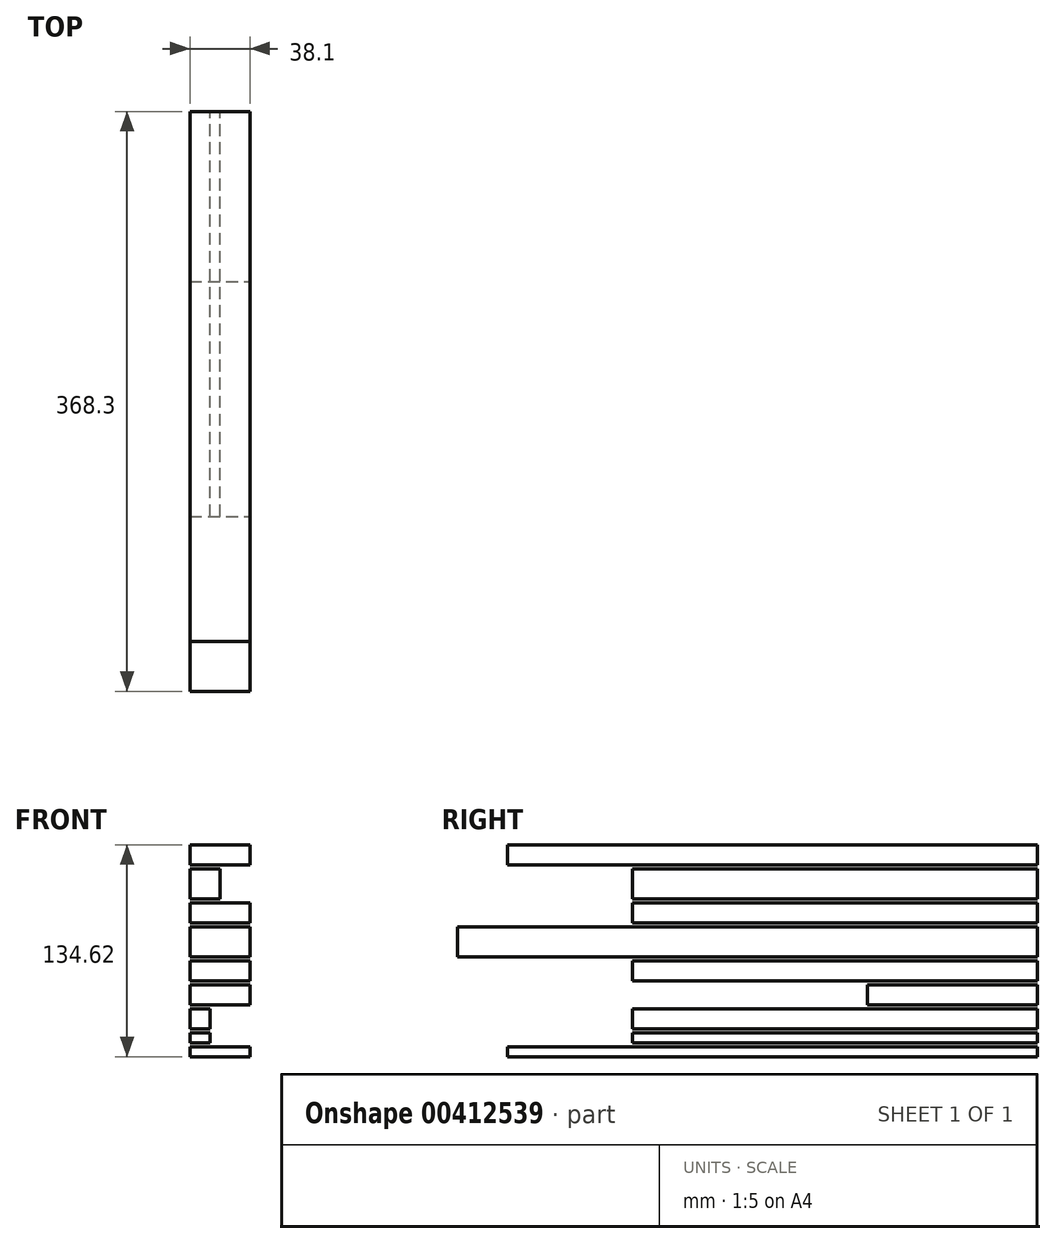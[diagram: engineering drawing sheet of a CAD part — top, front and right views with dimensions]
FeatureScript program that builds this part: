
annotation { "Feature Type Name" : "Feature", "Feature Type Description" : "" }
export const myFeature = defineFeature(function(context is Context, id is Id, definition is map)
    precondition{}
    {
        {
            var Q0;
            Q0=qCreatedBy(makeId("Front.planeOp"),FACE);
            var sketch = newSketch(context, id + "F0", { "sketchPlane" : qUnion([Q0])});
            skLineSegment(sketch, "E0.bottom", {"start": v(0, 0) * mm, "end": v(38.1, 0) * mm});
            skLineSegment(sketch, "E0.top", {"start": v(0, 19.05) * mm, "end": v(38.1, 19.05) * mm});
            skLineSegment(sketch, "E0.left", {"start": v(0, 0) * mm, "end": v(0, 19.05) * mm});
            skLineSegment(sketch, "E0.right", {"start": v(38.1, 0) * mm, "end": v(38.1, 19.05) * mm});
            skSolve(sketch);
        }
        {
            var Q0;
            Q0 = qSketchRegion(id + "F0", true);
            extrude(context, id + "F1", {"entities" : qUnion([Q0]), "depth" : 368.3 * mm});
        }
        {
            var Q0;
            Q0=qCreatedBy(makeId("Front.planeOp"),FACE);
            var sketch = newSketch(context, id + "F2", { "sketchPlane" : qUnion([Q0])});
            skLineSegment(sketch, "E1.bottom", {"start": v(0, 21.59) * mm, "end": v(38.1, 21.59) * mm});
            skLineSegment(sketch, "E1.top", {"start": v(0, 34.3) * mm, "end": v(38.1, 34.3) * mm});
            skLineSegment(sketch, "E1.left", {"start": v(0, 21.59) * mm, "end": v(0, 34.3) * mm});
            skLineSegment(sketch, "E1.right", {"start": v(38.1, 21.59) * mm, "end": v(38.1, 34.3) * mm});
            skSolve(sketch);
        }
        {
            var Q0;
            Q0 = qSketchRegion(id + "F2", true);
            extrude(context, id + "F3", {"entities" : qUnion([Q0]), "depth" : 257.18 * mm});
        }
        {
            var Q0;
            Q0=qCreatedBy(makeId("Front.planeOp"),FACE);
            var sketch = newSketch(context, id + "F4", { "sketchPlane" : qUnion([Q0])});
            skLineSegment(sketch, "E2.bottom", {"start": v(0, 36.83) * mm, "end": v(19.05, 36.83) * mm});
            skLineSegment(sketch, "E2.top", {"start": v(0, 55.88) * mm, "end": v(19.05, 55.88) * mm});
            skLineSegment(sketch, "E2.left", {"start": v(0, 36.83) * mm, "end": v(0, 55.88) * mm});
            skLineSegment(sketch, "E2.right", {"start": v(19.05, 36.83) * mm, "end": v(19.05, 55.88) * mm});
            skSolve(sketch);
        }
        {
            var Q0;
            Q0 = qSketchRegion(id + "F4", true);
            extrude(context, id + "F5", {"entities" : qUnion([Q0]), "depth" : 257.18 * mm});
        }
        {
            var Q0;
            Q0=qCreatedBy(makeId("Front.planeOp"),FACE);
            var sketch = newSketch(context, id + "F6", { "sketchPlane" : qUnion([Q0])});
            skLineSegment(sketch, "E3.bottom", {"start": v(0, 71.12) * mm, "end": v(38.1, 71.12) * mm});
            skLineSegment(sketch, "E3.top", {"start": v(0, 58.42) * mm, "end": v(38.1, 58.42) * mm});
            skLineSegment(sketch, "E3.left", {"start": v(0, 71.12) * mm, "end": v(0, 58.42) * mm});
            skLineSegment(sketch, "E3.right", {"start": v(38.1, 71.12) * mm, "end": v(38.1, 58.42) * mm});
            skSolve(sketch);
        }
        {
            var Q0;
            Q0 = qSketchRegion(id + "F6", true);
            extrude(context, id + "F7", {"entities" : qUnion([Q0]), "depth" : 336.55 * mm});
        }
        {
            var Q0;
            Q0=qCreatedBy(makeId("Front.planeOp"),FACE);
            var sketch = newSketch(context, id + "F8", { "sketchPlane" : qUnion([Q0])});
            skLineSegment(sketch, "E4.bottom", {"start": v(0, -2.54) * mm, "end": v(38.1, -2.54) * mm});
            skLineSegment(sketch, "E4.top", {"start": v(0, -15.24) * mm, "end": v(38.1, -15.24) * mm});
            skLineSegment(sketch, "E4.left", {"start": v(0, -2.54) * mm, "end": v(0, -15.24) * mm});
            skLineSegment(sketch, "E4.right", {"start": v(38.1, -2.54) * mm, "end": v(38.1, -15.24) * mm});
            skSolve(sketch);
        }
        {
            var Q0;
            Q0 = qSketchRegion(id + "F8", true);
            extrude(context, id + "F9", {"entities" : qUnion([Q0]), "depth" : 257.18 * mm});
        }
        {
            var Q0;
            Q0=qCreatedBy(makeId("Front.planeOp"),FACE);
            var sketch = newSketch(context, id + "F10", { "sketchPlane" : qUnion([Q0])});
            skLineSegment(sketch, "E5.bottom", {"start": v(0, -17.78) * mm, "end": v(38.1, -17.78) * mm});
            skLineSegment(sketch, "E5.top", {"start": v(0, -30.48) * mm, "end": v(38.1, -30.48) * mm});
            skLineSegment(sketch, "E5.left", {"start": v(0, -17.78) * mm, "end": v(0, -30.48) * mm});
            skLineSegment(sketch, "E5.right", {"start": v(38.1, -17.78) * mm, "end": v(38.1, -30.48) * mm});
            skSolve(sketch);
        }
        {
            var Q0;
            Q0 = qSketchRegion(id + "F10", true);
            extrude(context, id + "F11", {"entities" : qUnion([Q0]), "depth" : 107.95 * mm});
        }
        {
            var Q0;
            Q0=qCreatedBy(makeId("Front.planeOp"),FACE);
            var sketch = newSketch(context, id + "F12", { "sketchPlane" : qUnion([Q0])});
            skLineSegment(sketch, "E6.bottom", {"start": v(0, -33.02) * mm, "end": v(12.7, -33.02) * mm});
            skLineSegment(sketch, "E6.top", {"start": v(0, -45.72) * mm, "end": v(12.7, -45.72) * mm});
            skLineSegment(sketch, "E6.left", {"start": v(0, -33.02) * mm, "end": v(0, -45.72) * mm});
            skLineSegment(sketch, "E6.right", {"start": v(12.7, -33.02) * mm, "end": v(12.7, -45.72) * mm});
            skSolve(sketch);
        }
        {
            var Q0;
            Q0 = qSketchRegion(id + "F12", true);
            extrude(context, id + "F13", {"entities" : qUnion([Q0]), "depth" : 257.18 * mm});
        }
        {
            var Q0;
            Q0=qCreatedBy(makeId("Front.planeOp"),FACE);
            var sketch = newSketch(context, id + "F14", { "sketchPlane" : qUnion([Q0])});
            skLineSegment(sketch, "E7.bottom", {"start": v(0, -48.26) * mm, "end": v(12.7, -48.26) * mm});
            skLineSegment(sketch, "E7.top", {"start": v(0, -54.6) * mm, "end": v(12.7, -54.6) * mm});
            skLineSegment(sketch, "E7.left", {"start": v(0, -48.26) * mm, "end": v(0, -54.6) * mm});
            skLineSegment(sketch, "E7.right", {"start": v(12.7, -48.26) * mm, "end": v(12.7, -54.6) * mm});
            skSolve(sketch);
        }
        {
            var Q0;
            Q0 = qSketchRegion(id + "F14", true);
            extrude(context, id + "F15", {"entities" : qUnion([Q0]), "depth" : 257.18 * mm});
        }
        {
            var Q0;
            Q0=qCreatedBy(makeId("Front.planeOp"),FACE);
            var sketch = newSketch(context, id + "F16", { "sketchPlane" : qUnion([Q0])});
            skLineSegment(sketch, "E8.bottom", {"start": v(0, -57.15) * mm, "end": v(38.1, -57.15) * mm});
            skLineSegment(sketch, "E8.top", {"start": v(0, -63.5) * mm, "end": v(38.1, -63.5) * mm});
            skLineSegment(sketch, "E8.left", {"start": v(0, -57.15) * mm, "end": v(0, -63.5) * mm});
            skLineSegment(sketch, "E8.right", {"start": v(38.1, -57.15) * mm, "end": v(38.1, -63.5) * mm});
            skSolve(sketch);
        }
        {
            var Q0;
            Q0 = qSketchRegion(id + "F16", true);
            extrude(context, id + "F17", {"entities" : qUnion([Q0]), "depth" : 336.55 * mm});
        }
    });
